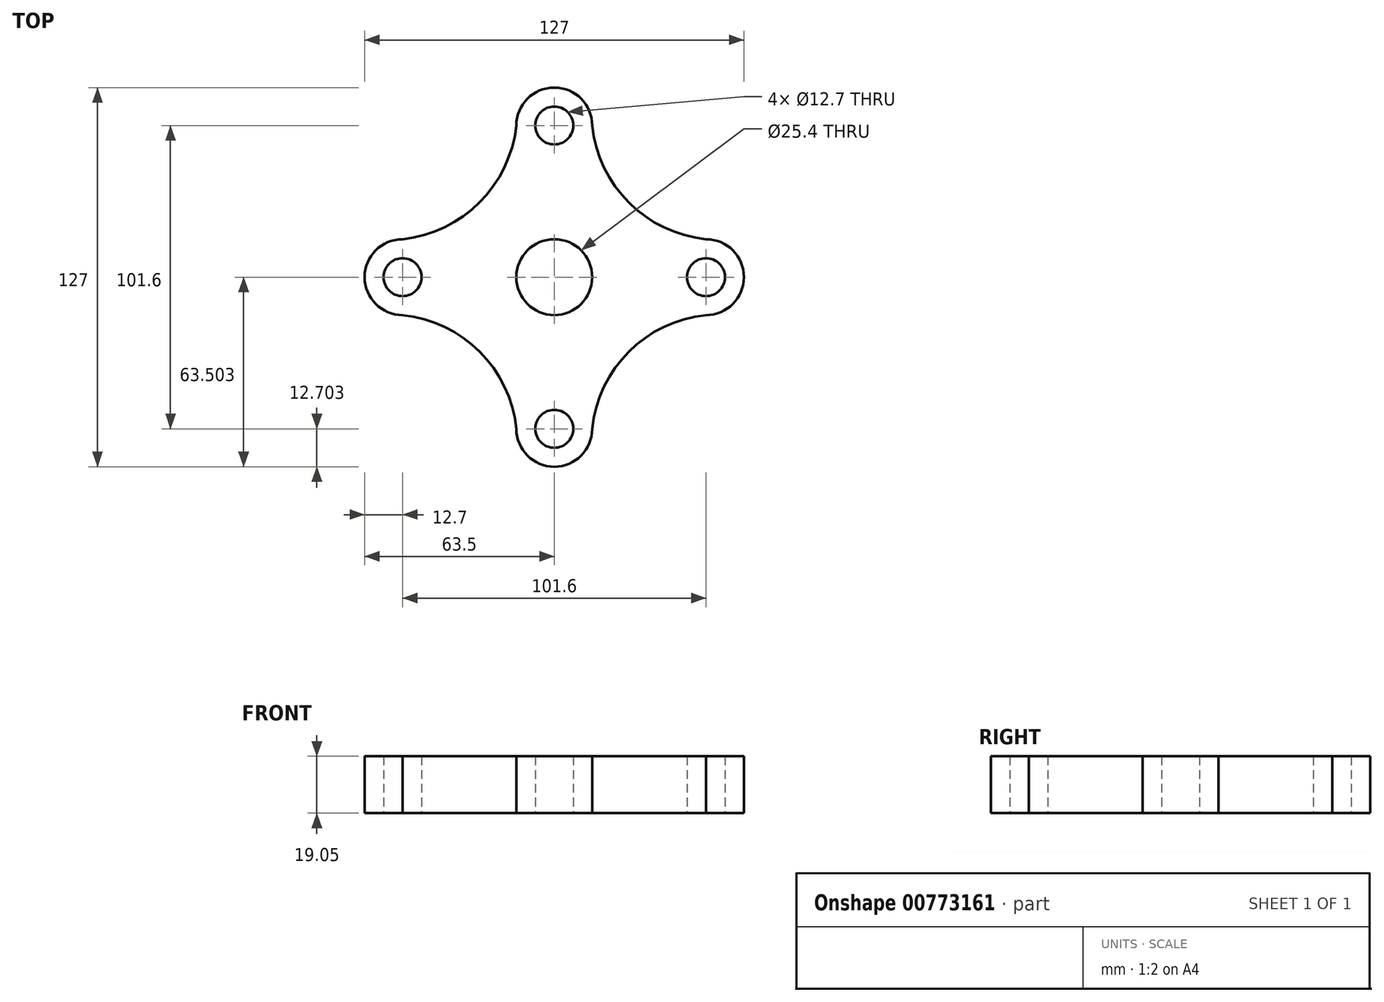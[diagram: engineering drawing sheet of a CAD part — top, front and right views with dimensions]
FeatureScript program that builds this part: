
annotation { "Feature Type Name" : "Feature", "Feature Type Description" : "" }
export const myFeature = defineFeature(function(context is Context, id is Id, definition is map)
    precondition{}
    {
        {
            var Q0;
            Q0=qCreatedBy(makeId("Top.planeOp"),FACE);
            var sketch = newSketch(context, id + "F0", { "sketchPlane" : qUnion([Q0])});
            skCircle(sketch, "E0", {"center": v(-50.92, -0.1) * mm, "radius": 6.35 * mm});
            skCircle(sketch, "E1", {"center": v(50.68, -0.1) * mm, "radius": 6.35 * mm});
            skCircle(sketch, "E2", {"center": v(-0.12, -0.1) * mm, "radius": 12.7 * mm});
            skCircle(sketch, "E3", {"center": v(-0.12, -50.9) * mm, "radius": 6.35 * mm});
            skCircle(sketch, "E4", {"center": v(-0.12, 50.7) * mm, "radius": 6.35 * mm});
            skArc(sketch, "E5", {"start": v(-50.92, 12.6) * mm, "mid": v(-25.15, 24.93) * mm, "end": v(-12.82, 50.7) * mm});
            skArc(sketch, "E6", {"start": v(12.58, 50.7) * mm, "mid": v(-0.12, 63.4) * mm, "end": v(-12.82, 50.7) * mm});
            skArc(sketch, "E7", {"start": v(-50.92, 12.6) * mm, "mid": v(-63.62, -0.1) * mm, "end": v(-50.92, -12.8) * mm});
            skPoint(sketch, "E8.trimOffspring.end.orphan", {"position": v(-50.92, 50.7) * mm});
            skArc(sketch, "E9", {"start": v(12.58, 50.7) * mm, "mid": v(24.86, 24.88) * mm, "end": v(50.68, 12.6) * mm});
            skArc(sketch, "E10", {"start": v(50.68, -12.8) * mm, "mid": v(63.38, -0.1) * mm, "end": v(50.68, 12.6) * mm});
            skPoint(sketch, "E11.orphan", {"position": v(50.68, 50.7) * mm});
            skArc(sketch, "E12", {"start": v(50.68, -12.8) * mm, "mid": v(24.86, -25.08) * mm, "end": v(12.58, -50.9) * mm});
            skArc(sketch, "E13", {"start": v(-12.82, -50.9) * mm, "mid": v(-0.12, -63.6) * mm, "end": v(12.58, -50.9) * mm});
            skArc(sketch, "E14", {"start": v(-12.82, -50.9) * mm, "mid": v(-25.1, -25.08) * mm, "end": v(-50.92, -12.8) * mm});
            skPoint(sketch, "E15.orphan", {"position": v(-50.92, -50.9) * mm});
            skPoint(sketch, "E16.orphan", {"position": v(50.68, -50.9) * mm});
            skSolve(sketch);
        }
        {
            var Q0;
            Q0=makeQuery(id+"F0.imprint","IMPRINT",FACE,{"disambiguationData":[TD([[makeQuery(id+"F0.imprint","IMPRINT",EDGE,{"derivedFrom":sQuery(id+"F0.wireOp",EDGE,"E0")}),-1.0]])]});
            extrude(context, id + "F1", {"entities" : qUnion([Q0]), "depth" : 19.05 * mm, "offsetDistance" : 25.4 * mm});
        }
    });
